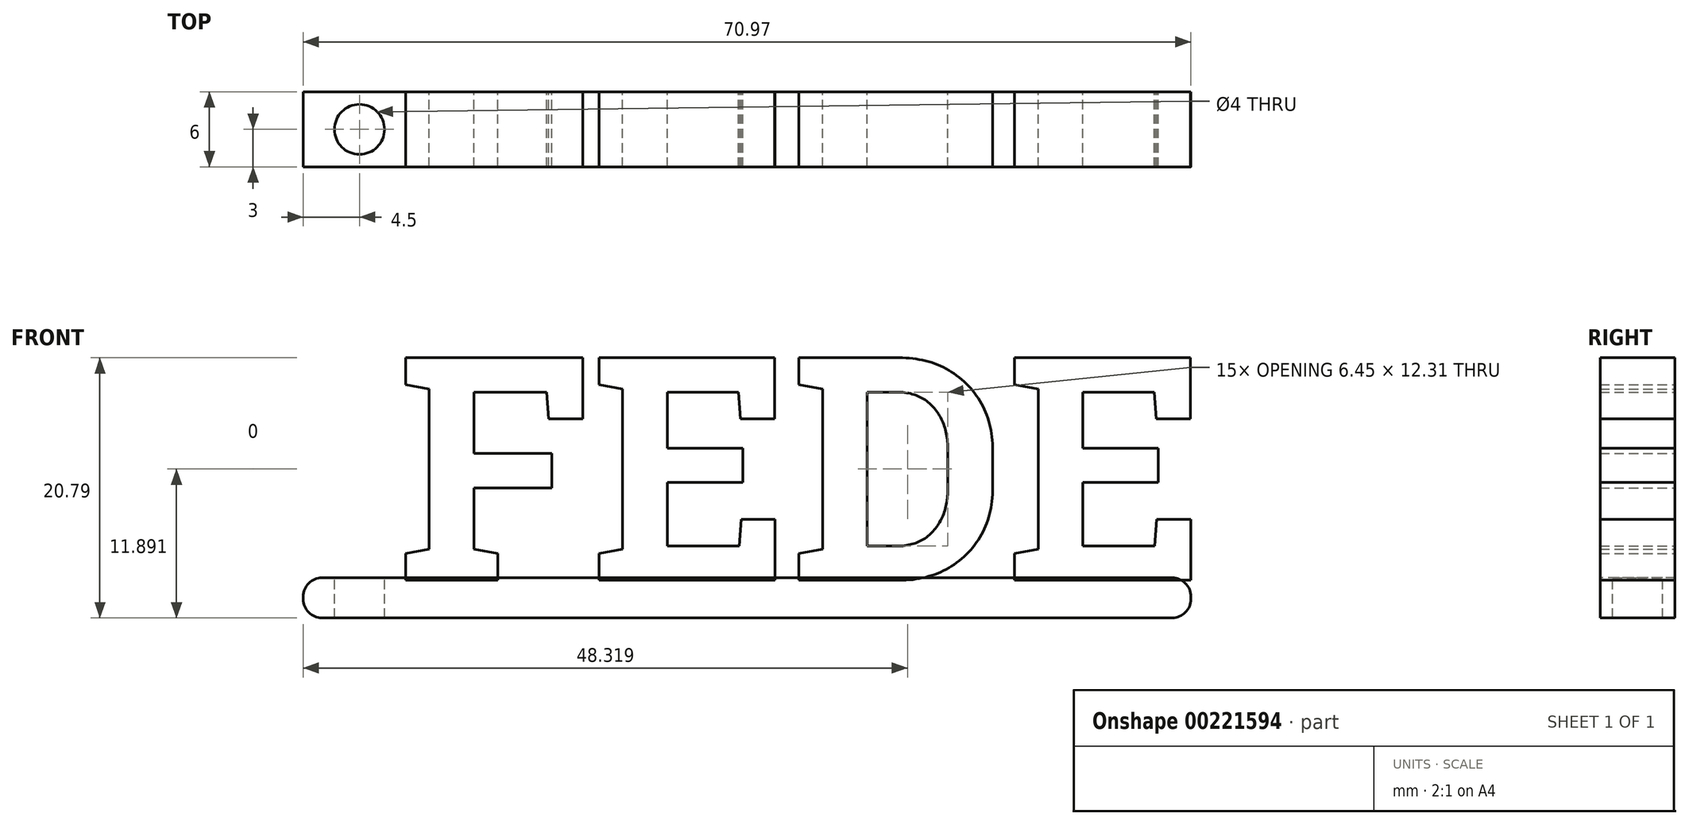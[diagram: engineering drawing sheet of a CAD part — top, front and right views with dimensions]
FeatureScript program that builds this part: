
annotation { "Feature Type Name" : "Feature", "Feature Type Description" : "" }
export const myFeature = defineFeature(function(context is Context, id is Id, definition is map)
    precondition{}
    {
        {
            var Q0;
            Q0=qCreatedBy(makeId("Front.planeOp"),FACE);
            var sketch = newSketch(context, id + "F0", { "sketchPlane" : qUnion([Q0])});
            skText(sketch, "E0", { "text": "FEDE", "fontName": "RobotoSlab-Bold.ttf"});
            const initialGuessF0  = {"E0": [-0.02, 0, 1, 0, 0.01802]};
            skSetInitialGuess(sketch, initialGuessF0);
            skSolve(sketch);
        }
        {
            var Q0;
            Q0=qSketchRegion(id+"F0",true);
            extrude(context, id + "F1", {"entities" : qUnion([Q0]), "endBound" : BoundingType.SYMMETRIC, "depth" : 6 * mm});
        }
        {
            var Q0;
            Q0=qCreatedBy(makeId("Top.planeOp"),FACE);
            var sketch = newSketch(context, id + "F2", { "sketchPlane" : qUnion([Q0])});
            skLineSegment(sketch, "E1.bottom", {"start": v(-20, 3) * mm, "end": v(43.47, 3) * mm});
            skLineSegment(sketch, "E1.top", {"start": v(-20, -3) * mm, "end": v(43.47, -3) * mm});
            skLineSegment(sketch, "E1.left", {"start": v(-20, 3) * mm, "end": v(-20, -3) * mm});
            skLineSegment(sketch, "E1.right", {"start": v(43.47, 3) * mm, "end": v(43.47, -3) * mm});
            skSolve(sketch);
        }
        {
            var Q0;
            Q0=makeQuery(id+"F2.imprint","IMPRINT",FACE,{"disambiguationData":[TD([[makeQuery(id+"F2.imprint","IMPRINT",EDGE,{"derivedFrom":sQuery(id+"F2.wireOp",EDGE,"E1.bottom")}),-1.0]])]});
            extrude(context, id + "F3", {"entities" : qUnion([Q0]), "depth" : 0.2 * mm});
        }
        {
            var Q0;
            Q0=makeQuery(id+"F3.opExtrude","CAP_FACE",FACE,{"disambiguationData":[OSD([sQuery(id+"F2.wireOp",EDGE,"E1.bottom"),sQuery(id+"F2.wireOp",EDGE,"E1.top"),sQuery(id+"F2.wireOp",EDGE,"E1.left"),sQuery(id+"F2.wireOp",EDGE,"E1.right")])],"isStart":true});
            extrude(context, id + "F4", {"entities" : qUnion([Q0]), "depth" : 3 * mm});
        }
        {
            var Q0;
            {var subQ0=sQuery(id+"F2.wireOp",EDGE,"E1.left");Q0=makeQuery(id+"FaVoHrOpcFZXiYX_6.opBoolean","MERGE",FACE,{"derivedFrom":[makeQuery(id+"F3.opExtrude","SWEPT_FACE",FACE,{"disambiguationData":[OSD([subQ0])]}),makeQuery(id+"F4.opExtrude","SWEPT_FACE",FACE,{"disambiguationData":[OSD([subQ0])]})]});}
            var sketch = newSketch(context, id + "F5", { "sketchPlane" : qUnion([Q0])});
            skLineSegment(sketch, "E2.bottom", {"start": v(-3, -3) * mm, "end": v(3, -3) * mm});
            skLineSegment(sketch, "E2.top", {"start": v(-3, 0.2) * mm, "end": v(3, 0.2) * mm});
            skLineSegment(sketch, "E2.left", {"start": v(-3, -3) * mm, "end": v(-3, 0.2) * mm});
            skLineSegment(sketch, "E2.right", {"start": v(3, -3) * mm, "end": v(3, 0.2) * mm});
            skSolve(sketch);
        }
        {
            var Q0;
            Q0=qSketchRegion(id+"F5",true);
            extrude(context, id + "F6", {"entities" : qUnion([Q0]), "operationType" : NewBodyOperationType.ADD, "depth" : 7.5 * mm});
        }
        {
            var Q0;
            Q0=makeQuery(id+"F6.opExtrude","CAP_EDGE",EDGE,{"disambiguationData":[OSD([sQuery(id+"F5.wireOp",EDGE,"E2.bottom")])],"isStart":false});
            var Q1;
            Q1=makeQuery(id+"F6.opExtrude","CAP_EDGE",EDGE,{"disambiguationData":[OSD([sQuery(id+"F5.wireOp",EDGE,"E2.top")])],"isStart":false});
            var Q2;
            Q2=makeQuery(id+"F4.opExtrude","CAP_EDGE",EDGE,{"disambiguationData":[OSD([sQuery(id+"F2.wireOp",EDGE,"E1.right")])],"isStart":false});
            fillet(context, id + "F7", {"entities" : qUnion([Q0, Q1, Q2]), "radius" : 1.5 * mm, "tangentPropagation" : true, "allowEdgeOverflow" : false});
        }
        {
            var Q0;
            {var subQ19=sQuery(id+"F2.wireOp",EDGE,"E1.top");var subQ20=sQuery(id+"F2.wireOp",EDGE,"E1.bottom");var subQ63=sQuery(id+"F0.wireOp",EDGE,"E0.sketch_text.stroke-2");var subQ66=sQuery(id+"F2.wireOp",EDGE,"E1.left");Q0=makeQuery(id+"F6.boolean.opBoolean","MERGE",FACE,{"derivedFrom":[makeQuery(id+"FaVoHrOpcFZXiYX_6.opBoolean","SPLIT",FACE,{"disambiguationData":[TD([makeQuery(id+"F1.opExtrude","SWEPT_FACE",FACE,{"disambiguationData":[OSD([subQ63])]})])],"derivedFrom":makeQuery(id+"F3.opExtrude","CAP_FACE",FACE,{"disambiguationData":[OSD([subQ20,subQ19,subQ66,sQuery(id+"F2.wireOp",EDGE,"E1.right")])],"isStart":false})}),makeQuery(id+"F6.opExtrude","SWEPT_FACE",FACE,{"disambiguationData":[OSD([sQuery(id+"F5.wireOp",EDGE,"E2.top")])]})]});}
            var sketch = newSketch(context, id + "F8", { "sketchPlane" : qUnion([Q0])});
            skCircle(sketch, "E3", {"center": v(-23, 0) * mm, "radius": 2 * mm});
            skSolve(sketch);
        }
        {
            var Q0;
            Q0=makeQuery(id+"F8.imprint","IMPRINT",FACE,{"disambiguationData":[TD([[makeQuery(id+"F8.imprint","IMPRINT",EDGE,{"derivedFrom":sQuery(id+"F8.wireOp",EDGE,"E3")}),1.0]])]});
            extrude(context, id + "F9", {"entities" : qUnion([Q0]), "operationType" : NewBodyOperationType.REMOVE, "oppositeDirection" : true, "depth" : 3.5 * mm});
        }
        {
            var Q0;
            Q0=makeQuery(id+"F3.opExtrude","CAP_EDGE",EDGE,{"disambiguationData":[OSD([sQuery(id+"F2.wireOp",EDGE,"E1.right")])],"isStart":false});
            fillet(context, id + "F10", {"entities" : qUnion([Q0]), "radius" : 1.5 * mm, "tangentPropagation" : true, "allowEdgeOverflow" : false});
        }
    });
